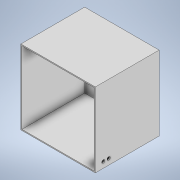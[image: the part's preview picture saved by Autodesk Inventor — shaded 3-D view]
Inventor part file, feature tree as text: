
AUTODESK INVENTOR PART (.ipt)
format: ipt  version: 2020 (Build 240168000, 168)  size: 124,416 bytes
history: native  units: mm
features: extrude x3, sketch x3, shell x1
ambient origin geometry x8: Origin, YZ Plane, XZ Plane, XY Plane, X Axis, Y Axis, Z Axis, Center Point
bodies: Solid1 (feature_tree)
feature tree (7):
  extrude  "Base"  Depth=350.0mm
  shell  "Shell1"  Thickness=300.0mm
  extrude  "Wire holes"  Depth=5.0mm
  extrude  "Exhaust"  Depth=350.0mm
  sketch  "Sketch2"  dims[d0=350.0mm d1=350.0mm d2=300.0mm d3=0.0mm]
  sketch  "Sketch3"  dims[d4=5.0mm d5=15.0mm]
  sketch  "Sketch4"  dims[d9=37.5mm d10=27.5mm d11=20.0mm d13=25.0mm d14=10.0mm d16=10.0mm d18=350.0mm d19=0.0mm d20=50.0mm d21=75.0mm d22=45.0deg d23=350.0mm d24=0.0mm]
